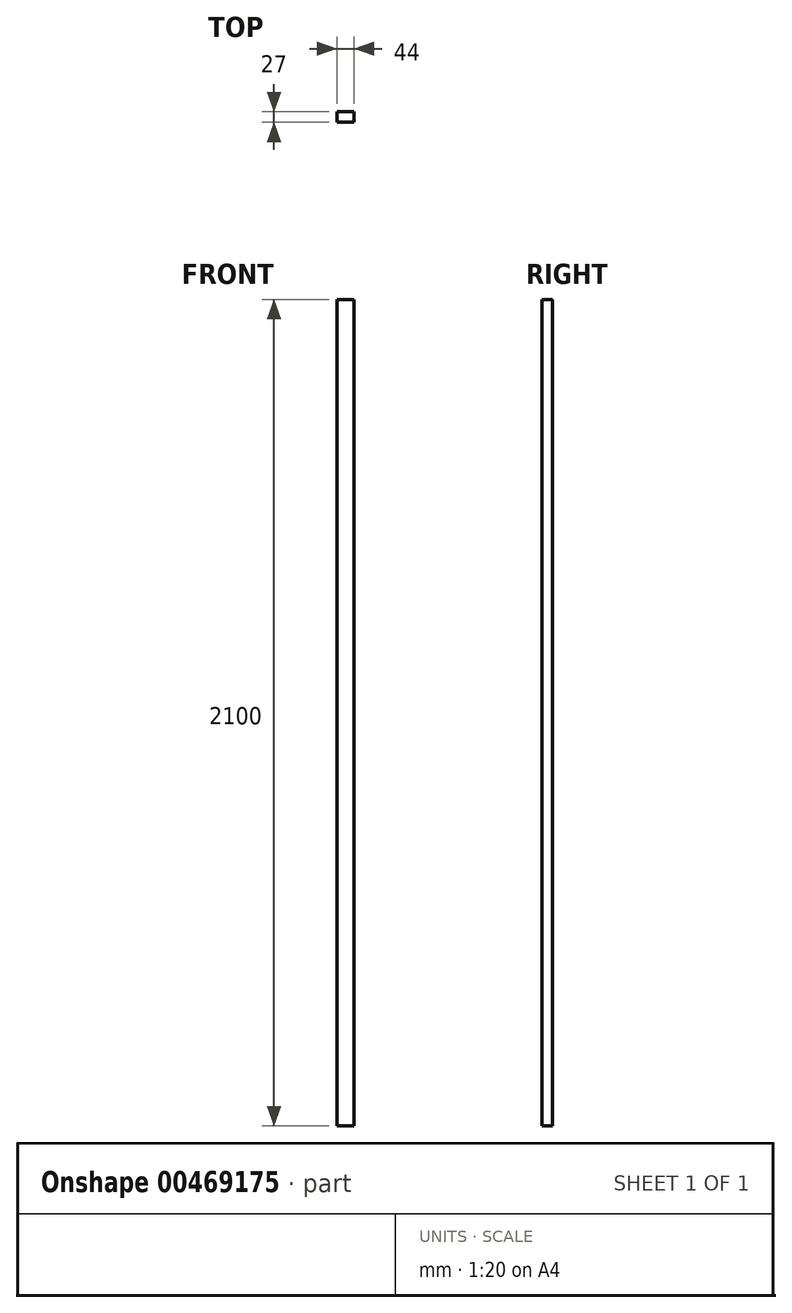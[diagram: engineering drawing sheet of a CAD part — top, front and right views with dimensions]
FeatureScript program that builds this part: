
annotation { "Feature Type Name" : "Feature", "Feature Type Description" : "" }
export const myFeature = defineFeature(function(context is Context, id is Id, definition is map)
    precondition{}
    {
        {
            var Q0;
            Q0=qCreatedBy(makeId("Top.planeOp"),FACE);
            var sketch = newSketch(context, id + "F0", { "sketchPlane" : qUnion([Q0])});
            skLineSegment(sketch, "E0.bottom", {"start": v(0, 27) * mm, "end": v(44, 27) * mm});
            skLineSegment(sketch, "E0.top", {"start": v(0, 0) * mm, "end": v(44, 0) * mm});
            skLineSegment(sketch, "E0.left", {"start": v(0, 27) * mm, "end": v(0, 0) * mm});
            skLineSegment(sketch, "E0.right", {"start": v(44, 27) * mm, "end": v(44, 0) * mm});
            skSolve(sketch);
        }
        {
            var Q0;
            Q0=makeQuery(id+"F0.imprint","IMPRINT",FACE,{"disambiguationData":[TD([[makeQuery(id+"F0.imprint","IMPRINT",EDGE,{"derivedFrom":sQuery(id+"F0.wireOp",EDGE,"E0.bottom")}),-1.0]])]});
            extrude(context, id + "F1", {"entities" : qUnion([Q0]), "depth" : 2100 * mm});
        }
    });
